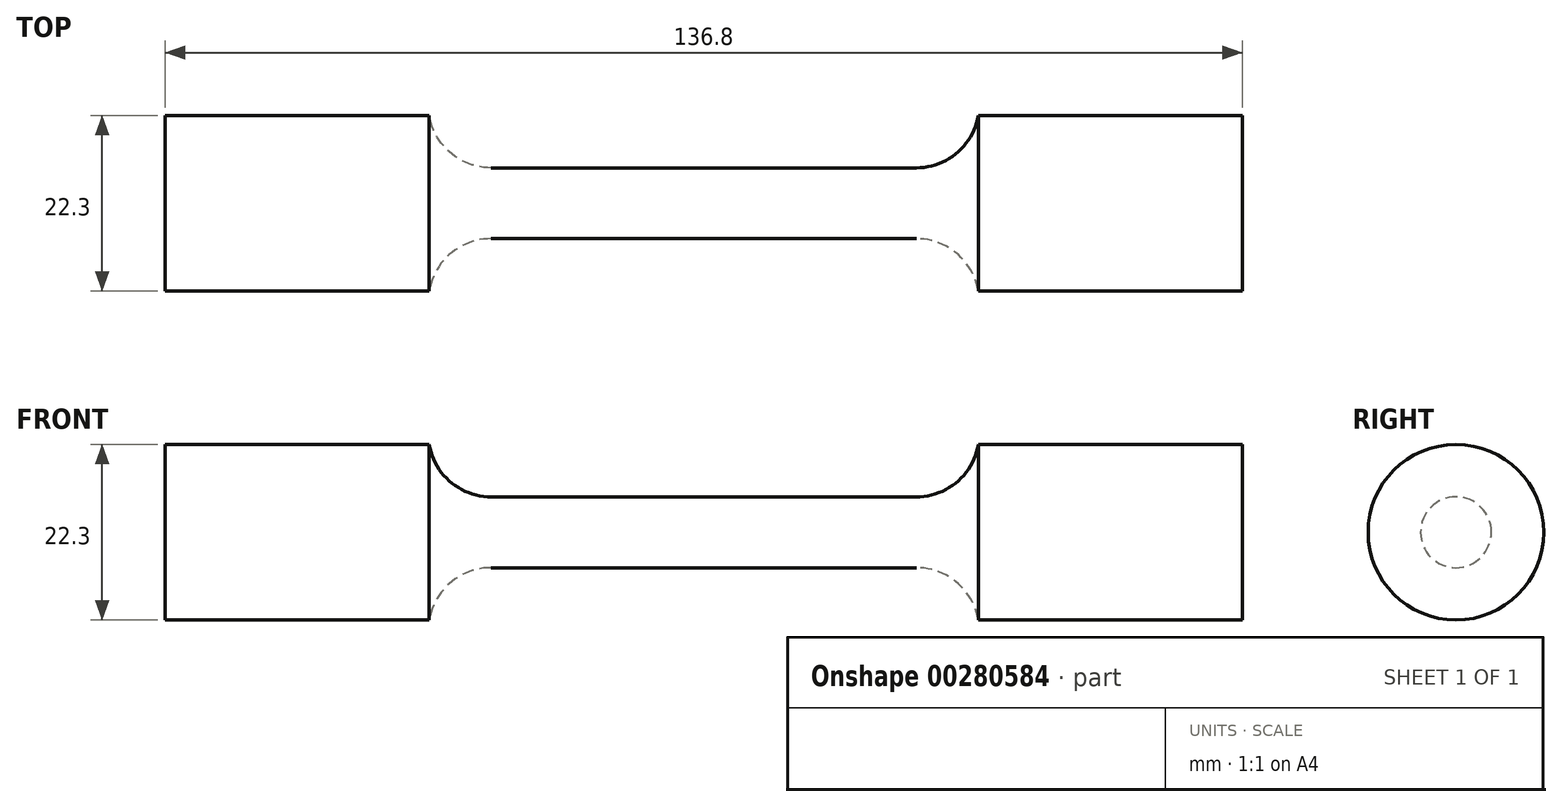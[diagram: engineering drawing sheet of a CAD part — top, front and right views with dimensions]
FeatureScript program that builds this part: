
annotation { "Feature Type Name" : "Feature", "Feature Type Description" : "" }
export const myFeature = defineFeature(function(context is Context, id is Id, definition is map)
    precondition{}
    {
        {
            var Q0;
            Q0=qCreatedBy(makeId("Front.planeOp"),FACE);
            var sketch = newSketch(context, id + "F0", { "sketchPlane" : qUnion([Q0])});
            skLineSegment(sketch, "E0", {"start": v(0, 4.5) * mm, "end": v(27, 4.5) * mm});
            skArc(sketch, "E1", {"start": v(27, 4.5) * mm, "mid": v(32.16, 6.39) * mm, "end": v(34.89, 11.15) * mm});
            skLineSegment(sketch, "E2", {"start": v(34.89, 11.15) * mm, "end": v(68.4, 11.15) * mm});
            skLineSegment(sketch, "E3", {"start": v(68.4, 11.15) * mm, "end": v(68.4, 0) * mm});
            skLineSegment(sketch, "E4.MirrorCS", {"start": v(0, 4.5) * mm, "end": v(-27, 4.5) * mm});
            skLineSegment(sketch, "E5.MirrorCS", {"start": v(-68.4, 11.15) * mm, "end": v(-68.4, 0) * mm});
            skLineSegment(sketch, "E6.MirrorCS", {"start": v(-34.89, 11.15) * mm, "end": v(-68.4, 11.15) * mm});
            skArc(sketch, "E7.MirrorCS", {"start": v(-27, 4.5) * mm, "mid": v(-32.16, 6.39) * mm, "end": v(-34.89, 11.15) * mm});
            skLineSegment(sketch, "E8", {"start": v(-68.4, 0) * mm, "end": v(68.4, 0) * mm});
            skSolve(sketch);
        }
        {
            var Q0;
            Q0 = qSketchRegion(id + "F0", true);
            var Q1;
            Q1=sQuery(id+"F0.wireOp",EDGE,"E8");
            revolve(context, id + "F1", {"entities" : qUnion([Q0]), "axis" : qUnion([Q1]), "revolveType" : RevolveType.FULL});
        }
    });
